# Revit family: Shower-Shower_Trim-KOHLER-Loure-K-T14665
name_source: partatom
category: Plumbing Fixtures
revit_build: Autodesk Revit 2015 (Build: 20140606_1530(x64)
units: mm (PartAtom-declared; Revit-internal decimal feet)

## types (5) — shared parameters
ADA Compliant = No
Assembly Code = D2010700
CW Connection = No
Cold Water Inlet = Cold Water Inlet
Date Modified = 03/22/2019
Default Elevation = 42"
Drain Included = No
Flow Rate = 0 GPM
HW Connection = Yes
Height = 6 1/4"
Manufacturer = KOHLER Co.
MasterFormat 1995 = 15410
MasterFormat 2004 = 22.41.23
Material = Premium Material Construction
Panel Thickness = 0"
Pressure = 0.00 psi
Product Documentation Link = https://www.us.kohler.com
Product Name = Loure
Product Page URL = http://www.us.kohler.com
Tempered Water Inlet = Tempered Water Inlet
URL = https://www.us.kohler.com
Vent Connection = No
Waste Connection = No
Waste Water Outlet = Waste Water Outlet
WaterSense Certified = No
Width = 6 1/4"

## per-type parameters (varying)
| type | Description | Distance 1 | Finish | Length | Model | Type | With_Shower_Head | Withou_Shower_Head |
| Without_Shower_Head, CP-Polished Chrome | Rite-Temperature shower trim set with push-button diverter, less showerhead | 1 1/4" | Kohler-Metal-CP-Polished_Chrome | 8 5/16" | K-T14665-4L-CP | 1 | No | Yes |
| Without_Shower_Head, SN-Vibrant Polished Nickel | Rite-Temperature shower trim set with push-button diverter, less showerhead | 1 1/4" | Kohler-Metal-SN-Vibrant_Polished_Nickel | 8 5/16" | K-T14665-4L-SN | 2 | No | Yes |
| Without_Shower_Head, BN-Vibrant Brushed Nickel | Rite-Temperature shower trim set with push-button diverter, less showerhead | 1 1/4" | Kohler-Metal-BN-Vibrant_Brushed_Nickel | 8 5/16" | K-T14665-4L-BN | 3 | No | Yes |
| With_Shower_Head, CP-Polished Chrome | Rite-Temperatue shower trim with diverter | 3 1/2" | Kohler-Metal-CP-Polished_Chrome | 10 1/8" | K-T14665-4-CP | 4 | Yes | No |
| With_Shower_Head, BN-Vibrant Brushed Nickel | Rite-Temperatue shower trim with diverter | 3 1/2" | Kohler-Metal-BN-Vibrant_Brushed_Nickel | 10 1/8" | K-T14665-4-BN | 5 | Yes | No |

## geometry (parser evidence)
native form markers: Sweep x8
no freeform markers — native parametric forms only
